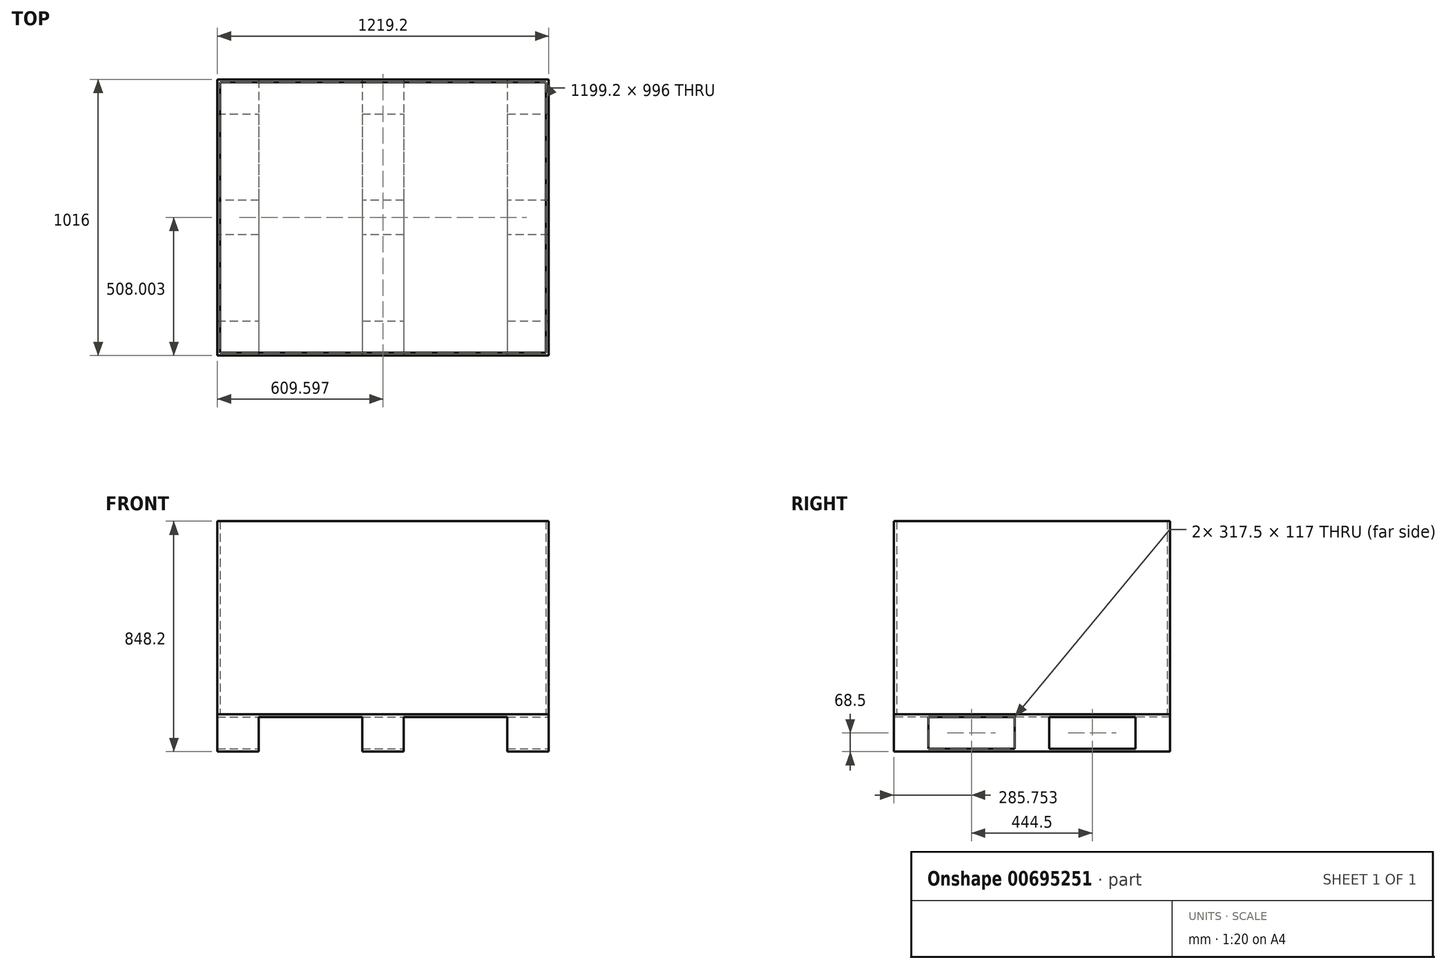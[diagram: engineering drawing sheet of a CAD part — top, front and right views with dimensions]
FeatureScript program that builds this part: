
annotation { "Feature Type Name" : "Feature", "Feature Type Description" : "" }
export const myFeature = defineFeature(function(context is Context, id is Id, definition is map)
    precondition{}
    {
        {
            var Q0;
            Q0=qCreatedBy(makeId("Top.planeOp"),FACE);
            var sketch = newSketch(context, id + "F0", { "sketchPlane" : qUnion([Q0])});
            skLineSegment(sketch, "E0.bottom", {"start": v(-1162.93, 976.86) * mm, "end": v(56.27, 976.86) * mm});
            skLineSegment(sketch, "E0.top", {"start": v(-1162.93, -39.14) * mm, "end": v(56.27, -39.14) * mm});
            skLineSegment(sketch, "E0.left", {"start": v(-1162.93, 976.86) * mm, "end": v(-1162.93, -39.14) * mm});
            skLineSegment(sketch, "E0.right", {"start": v(56.27, 976.86) * mm, "end": v(56.27, -39.14) * mm});
            skLineSegment(sketch, "E1.0", {"start": v(-1010.53, 976.86) * mm, "end": v(-1010.53, -39.14) * mm});
            skLineSegment(sketch, "E2.0", {"start": v(-96.13, 976.86) * mm, "end": v(-96.13, -39.14) * mm});
            skLineSegment(sketch, "E3.0", {"start": v(-1162.93, 849.86) * mm, "end": v(56.27, 849.86) * mm});
            skLineSegment(sketch, "E4.0", {"start": v(-1162.93, 87.86) * mm, "end": v(56.27, 87.86) * mm});
            skLineSegment(sketch, "E5", {"start": v(-553.33, 976.86) * mm, "end": v(-553.33, -39.14) * mm, "construction": true});
            skLineSegment(sketch, "E6", {"start": v(56.27, 468.86) * mm, "end": v(-1162.93, 468.86) * mm, "construction": true});
            skLineSegment(sketch, "E7.0", {"start": v(56.27, 532.36) * mm, "end": v(-1162.93, 532.36) * mm});
            skLineSegment(sketch, "E8.0", {"start": v(56.27, 405.36) * mm, "end": v(-1162.93, 405.36) * mm});
            skLineSegment(sketch, "E9.0", {"start": v(-629.53, 976.86) * mm, "end": v(-629.53, -39.14) * mm});
            skLineSegment(sketch, "E10.0", {"start": v(-477.13, 976.86) * mm, "end": v(-477.13, -39.14) * mm});
            skSolve(sketch);
        }
        {
            var Q0;
            {var subQ0=sQuery(id+"F0.wireOp",EDGE,"E0.left");var subQ1=sQuery(id+"F0.wireOp",EDGE,"E0.bottom");var subQ2=makeQuery(id+"F0.imprint","INTERSECT",VERTEX,{"derivedFrom":[subQ1,subQ0]});Q0=makeQuery(id+"F0.imprint","IMPRINT",FACE,{"disambiguationData":[TD([[makeQuery(id+"F0.imprint","IMPRINT",EDGE,{"disambiguationData":[TD([[subQ2,-1.0]])],"derivedFrom":subQ1}),-1.0]])]});}
            var Q1;
            {var subQ0=sQuery(id+"F0.wireOp",EDGE,"E1.0");var subQ1=sQuery(id+"F0.wireOp",EDGE,"E0.bottom");var subQ2=makeQuery(id+"F0.imprint","INTERSECT",VERTEX,{"derivedFrom":[subQ1,subQ0]});Q1=makeQuery(id+"F0.imprint","IMPRINT",FACE,{"disambiguationData":[TD([[makeQuery(id+"F0.imprint","IMPRINT",EDGE,{"disambiguationData":[TD([[subQ2,-1.0]])],"derivedFrom":subQ1}),-1.0]])]});}
            var Q2;
            {var subQ0=sQuery(id+"F0.wireOp",EDGE,"E9.0");var subQ1=sQuery(id+"F0.wireOp",EDGE,"E0.bottom");var subQ2=makeQuery(id+"F0.imprint","INTERSECT",VERTEX,{"derivedFrom":[subQ1,subQ0]});Q2=makeQuery(id+"F0.imprint","IMPRINT",FACE,{"disambiguationData":[TD([[makeQuery(id+"F0.imprint","IMPRINT",EDGE,{"disambiguationData":[TD([[subQ2,-1.0]])],"derivedFrom":subQ1}),-1.0]])]});}
            var Q3;
            {var subQ0=sQuery(id+"F0.wireOp",EDGE,"E2.0");var subQ1=sQuery(id+"F0.wireOp",EDGE,"E0.bottom");var subQ2=makeQuery(id+"F0.imprint","INTERSECT",VERTEX,{"derivedFrom":[subQ1,subQ0]});Q3=makeQuery(id+"F0.imprint","IMPRINT",FACE,{"disambiguationData":[TD([[makeQuery(id+"F0.imprint","IMPRINT",EDGE,{"disambiguationData":[TD([[subQ2,1.0]])],"derivedFrom":subQ1}),-1.0]])]});}
            var Q4;
            {var subQ0=sQuery(id+"F0.wireOp",EDGE,"E0.right");var subQ1=sQuery(id+"F0.wireOp",EDGE,"E0.bottom");var subQ2=makeQuery(id+"F0.imprint","INTERSECT",VERTEX,{"derivedFrom":[subQ1,subQ0]});Q4=makeQuery(id+"F0.imprint","IMPRINT",FACE,{"disambiguationData":[TD([[makeQuery(id+"F0.imprint","IMPRINT",EDGE,{"disambiguationData":[TD([[subQ2,1.0]])],"derivedFrom":subQ1}),-1.0]])]});}
            var Q5;
            {var subQ0=sQuery(id+"F0.wireOp",EDGE,"E3.0");var subQ1=sQuery(id+"F0.wireOp",EDGE,"E0.right");var subQ2=makeQuery(id+"F0.imprint","INTERSECT",VERTEX,{"derivedFrom":[subQ1,subQ0]});Q5=makeQuery(id+"F0.imprint","IMPRINT",FACE,{"disambiguationData":[TD([[makeQuery(id+"F0.imprint","IMPRINT",EDGE,{"disambiguationData":[TD([[subQ2,-1.0]])],"derivedFrom":subQ1}),-1.0]])]});}
            var Q6;
            {var subQ0=sQuery(id+"F0.wireOp",EDGE,"E3.0");var subQ1=sQuery(id+"F0.wireOp",EDGE,"E2.0");var subQ2=makeQuery(id+"F0.imprint","INTERSECT",VERTEX,{"derivedFrom":[subQ1,subQ0]});Q6=makeQuery(id+"F0.imprint","IMPRINT",FACE,{"disambiguationData":[TD([[makeQuery(id+"F0.imprint","IMPRINT",EDGE,{"disambiguationData":[TD([[subQ2,-1.0]])],"derivedFrom":subQ1}),-1.0]])]});}
            var Q7;
            {var subQ0=sQuery(id+"F0.wireOp",EDGE,"E9.0");var subQ1=sQuery(id+"F0.wireOp",EDGE,"E3.0");var subQ2=makeQuery(id+"F0.imprint","INTERSECT",VERTEX,{"derivedFrom":[subQ1,subQ0]});Q7=makeQuery(id+"F0.imprint","IMPRINT",FACE,{"disambiguationData":[TD([[makeQuery(id+"F0.imprint","IMPRINT",EDGE,{"disambiguationData":[TD([[subQ2,-1.0]])],"derivedFrom":subQ1}),-1.0]])]});}
            var Q8;
            {var subQ0=sQuery(id+"F0.wireOp",EDGE,"E3.0");var subQ1=sQuery(id+"F0.wireOp",EDGE,"E1.0");var subQ2=makeQuery(id+"F0.imprint","INTERSECT",VERTEX,{"derivedFrom":[subQ1,subQ0]});Q8=makeQuery(id+"F0.imprint","IMPRINT",FACE,{"disambiguationData":[TD([[makeQuery(id+"F0.imprint","IMPRINT",EDGE,{"disambiguationData":[TD([[subQ2,-1.0]])],"derivedFrom":subQ1}),1.0]])]});}
            var Q9;
            {var subQ0=sQuery(id+"F0.wireOp",EDGE,"E3.0");var subQ1=sQuery(id+"F0.wireOp",EDGE,"E0.left");var subQ2=makeQuery(id+"F0.imprint","INTERSECT",VERTEX,{"derivedFrom":[subQ1,subQ0]});Q9=makeQuery(id+"F0.imprint","IMPRINT",FACE,{"disambiguationData":[TD([[makeQuery(id+"F0.imprint","IMPRINT",EDGE,{"disambiguationData":[TD([[subQ2,-1.0]])],"derivedFrom":subQ1}),1.0]])]});}
            var Q10;
            {var subQ0=sQuery(id+"F0.wireOp",EDGE,"E0.left");var subQ1=sQuery(id+"F0.wireOp",EDGE,"E0.top");var subQ2=makeQuery(id+"F0.imprint","INTERSECT",VERTEX,{"derivedFrom":[subQ1,subQ0]});Q10=makeQuery(id+"F0.imprint","IMPRINT",FACE,{"disambiguationData":[TD([[makeQuery(id+"F0.imprint","IMPRINT",EDGE,{"disambiguationData":[TD([[subQ2,-1.0]])],"derivedFrom":subQ1}),1.0]])]});}
            var Q11;
            {var subQ0=sQuery(id+"F0.wireOp",EDGE,"E4.0");var subQ1=sQuery(id+"F0.wireOp",EDGE,"E0.left");var subQ2=makeQuery(id+"F0.imprint","INTERSECT",VERTEX,{"derivedFrom":[subQ1,subQ0]});Q11=makeQuery(id+"F0.imprint","IMPRINT",FACE,{"disambiguationData":[TD([[makeQuery(id+"F0.imprint","IMPRINT",EDGE,{"disambiguationData":[TD([[subQ2,1.0]])],"derivedFrom":subQ1}),1.0]])]});}
            var Q12;
            {var subQ0=sQuery(id+"F0.wireOp",EDGE,"E1.0");var subQ1=sQuery(id+"F0.wireOp",EDGE,"E0.top");var subQ2=makeQuery(id+"F0.imprint","INTERSECT",VERTEX,{"derivedFrom":[subQ1,subQ0]});Q12=makeQuery(id+"F0.imprint","IMPRINT",FACE,{"disambiguationData":[TD([[makeQuery(id+"F0.imprint","IMPRINT",EDGE,{"disambiguationData":[TD([[subQ2,-1.0]])],"derivedFrom":subQ1}),1.0]])]});}
            var Q13;
            {var subQ0=sQuery(id+"F0.wireOp",EDGE,"E8.0");var subQ1=sQuery(id+"F0.wireOp",EDGE,"E2.0");var subQ2=makeQuery(id+"F0.imprint","INTERSECT",VERTEX,{"derivedFrom":[subQ1,subQ0]});Q13=makeQuery(id+"F0.imprint","IMPRINT",FACE,{"disambiguationData":[TD([[makeQuery(id+"F0.imprint","IMPRINT",EDGE,{"disambiguationData":[TD([[subQ2,-1.0]])],"derivedFrom":subQ1}),-1.0]])]});}
            var Q14;
            {var subQ0=sQuery(id+"F0.wireOp",EDGE,"E8.0");var subQ1=sQuery(id+"F0.wireOp",EDGE,"E1.0");var subQ2=makeQuery(id+"F0.imprint","INTERSECT",VERTEX,{"derivedFrom":[subQ1,subQ0]});Q14=makeQuery(id+"F0.imprint","IMPRINT",FACE,{"disambiguationData":[TD([[makeQuery(id+"F0.imprint","IMPRINT",EDGE,{"disambiguationData":[TD([[subQ2,-1.0]])],"derivedFrom":subQ1}),1.0]])]});}
            var Q15;
            {var subQ0=sQuery(id+"F0.wireOp",EDGE,"E2.0");var subQ1=sQuery(id+"F0.wireOp",EDGE,"E0.top");var subQ2=makeQuery(id+"F0.imprint","INTERSECT",VERTEX,{"derivedFrom":[subQ1,subQ0]});Q15=makeQuery(id+"F0.imprint","IMPRINT",FACE,{"disambiguationData":[TD([[makeQuery(id+"F0.imprint","IMPRINT",EDGE,{"disambiguationData":[TD([[subQ2,1.0]])],"derivedFrom":subQ1}),1.0]])]});}
            var Q16;
            {var subQ0=sQuery(id+"F0.wireOp",EDGE,"E4.0");var subQ1=sQuery(id+"F0.wireOp",EDGE,"E0.right");var subQ2=makeQuery(id+"F0.imprint","INTERSECT",VERTEX,{"derivedFrom":[subQ1,subQ0]});Q16=makeQuery(id+"F0.imprint","IMPRINT",FACE,{"disambiguationData":[TD([[makeQuery(id+"F0.imprint","IMPRINT",EDGE,{"disambiguationData":[TD([[subQ2,1.0]])],"derivedFrom":subQ1}),-1.0]])]});}
            var Q17;
            {var subQ0=sQuery(id+"F0.wireOp",EDGE,"E7.0");var subQ1=sQuery(id+"F0.wireOp",EDGE,"E0.left");var subQ2=makeQuery(id+"F0.imprint","INTERSECT",VERTEX,{"derivedFrom":[subQ1,subQ0]});Q17=makeQuery(id+"F0.imprint","IMPRINT",FACE,{"disambiguationData":[TD([[makeQuery(id+"F0.imprint","IMPRINT",EDGE,{"disambiguationData":[TD([[subQ2,-1.0]])],"derivedFrom":subQ1}),1.0]])]});}
            var Q18;
            {var subQ0=sQuery(id+"F0.wireOp",EDGE,"E7.0");var subQ1=sQuery(id+"F0.wireOp",EDGE,"E1.0");var subQ2=makeQuery(id+"F0.imprint","INTERSECT",VERTEX,{"derivedFrom":[subQ1,subQ0]});Q18=makeQuery(id+"F0.imprint","IMPRINT",FACE,{"disambiguationData":[TD([[makeQuery(id+"F0.imprint","IMPRINT",EDGE,{"disambiguationData":[TD([[subQ2,-1.0]])],"derivedFrom":subQ1}),1.0]])]});}
            var Q19;
            {var subQ0=sQuery(id+"F0.wireOp",EDGE,"E10.0");var subQ1=sQuery(id+"F0.wireOp",EDGE,"E7.0");var subQ2=makeQuery(id+"F0.imprint","INTERSECT",VERTEX,{"derivedFrom":[subQ1,subQ0]});Q19=makeQuery(id+"F0.imprint","IMPRINT",FACE,{"disambiguationData":[TD([[makeQuery(id+"F0.imprint","IMPRINT",EDGE,{"disambiguationData":[TD([[subQ2,-1.0]])],"derivedFrom":subQ1}),1.0]])]});}
            var Q20;
            {var subQ0=sQuery(id+"F0.wireOp",EDGE,"E7.0");var subQ1=sQuery(id+"F0.wireOp",EDGE,"E2.0");var subQ2=makeQuery(id+"F0.imprint","INTERSECT",VERTEX,{"derivedFrom":[subQ1,subQ0]});Q20=makeQuery(id+"F0.imprint","IMPRINT",FACE,{"disambiguationData":[TD([[makeQuery(id+"F0.imprint","IMPRINT",EDGE,{"disambiguationData":[TD([[subQ2,-1.0]])],"derivedFrom":subQ1}),-1.0]])]});}
            var Q21;
            {var subQ0=sQuery(id+"F0.wireOp",EDGE,"E9.0");var subQ1=sQuery(id+"F0.wireOp",EDGE,"E4.0");var subQ2=makeQuery(id+"F0.imprint","INTERSECT",VERTEX,{"derivedFrom":[subQ1,subQ0]});Q21=makeQuery(id+"F0.imprint","IMPRINT",FACE,{"disambiguationData":[TD([[makeQuery(id+"F0.imprint","IMPRINT",EDGE,{"disambiguationData":[TD([[subQ2,-1.0]])],"derivedFrom":subQ1}),1.0]])]});}
            var Q22;
            {var subQ0=sQuery(id+"F0.wireOp",EDGE,"E7.0");var subQ1=sQuery(id+"F0.wireOp",EDGE,"E0.right");var subQ2=makeQuery(id+"F0.imprint","INTERSECT",VERTEX,{"derivedFrom":[subQ1,subQ0]});Q22=makeQuery(id+"F0.imprint","IMPRINT",FACE,{"disambiguationData":[TD([[makeQuery(id+"F0.imprint","IMPRINT",EDGE,{"disambiguationData":[TD([[subQ2,-1.0]])],"derivedFrom":subQ1}),-1.0]])]});}
            var Q23;
            {var subQ0=sQuery(id+"F0.wireOp",EDGE,"E9.0");var subQ1=sQuery(id+"F0.wireOp",EDGE,"E0.top");var subQ2=makeQuery(id+"F0.imprint","INTERSECT",VERTEX,{"derivedFrom":[subQ1,subQ0]});Q23=makeQuery(id+"F0.imprint","IMPRINT",FACE,{"disambiguationData":[TD([[makeQuery(id+"F0.imprint","IMPRINT",EDGE,{"disambiguationData":[TD([[subQ2,-1.0]])],"derivedFrom":subQ1}),1.0]])]});}
            var Q24;
            {var subQ0=sQuery(id+"F0.wireOp",EDGE,"E0.right");var subQ1=sQuery(id+"F0.wireOp",EDGE,"E0.top");var subQ2=makeQuery(id+"F0.imprint","INTERSECT",VERTEX,{"derivedFrom":[subQ1,subQ0]});Q24=makeQuery(id+"F0.imprint","IMPRINT",FACE,{"disambiguationData":[TD([[makeQuery(id+"F0.imprint","IMPRINT",EDGE,{"disambiguationData":[TD([[subQ2,1.0]])],"derivedFrom":subQ1}),1.0]])]});}
            extrude(context, id + "F1", {"entities" : qUnion([Q0, Q1, Q2, Q3, Q4, Q5, Q6, Q7, Q8, Q9, Q10, Q11, Q12, Q13, Q14, Q15, Q16, Q17, Q18, Q19, Q20, Q21, Q22, Q23, Q24]), "depth" : 10 * mm, "offsetDistance" : 25 * mm});
        }
        {
            var Q0;
            {var subQ0=sQuery(id+"F0.wireOp",EDGE,"E0.left");var subQ1=sQuery(id+"F0.wireOp",EDGE,"E0.top");var subQ2=makeQuery(id+"F0.imprint","INTERSECT",VERTEX,{"derivedFrom":[subQ1,subQ0]});Q0=makeQuery(id+"F0.imprint","IMPRINT",FACE,{"disambiguationData":[TD([[makeQuery(id+"F0.imprint","IMPRINT",EDGE,{"disambiguationData":[TD([[subQ2,-1.0]])],"derivedFrom":subQ1}),1.0]])]});}
            var Q1;
            {var subQ0=sQuery(id+"F0.wireOp",EDGE,"E9.0");var subQ1=sQuery(id+"F0.wireOp",EDGE,"E0.top");var subQ2=makeQuery(id+"F0.imprint","INTERSECT",VERTEX,{"derivedFrom":[subQ1,subQ0]});Q1=makeQuery(id+"F0.imprint","IMPRINT",FACE,{"disambiguationData":[TD([[makeQuery(id+"F0.imprint","IMPRINT",EDGE,{"disambiguationData":[TD([[subQ2,-1.0]])],"derivedFrom":subQ1}),1.0]])]});}
            var Q2;
            {var subQ0=sQuery(id+"F0.wireOp",EDGE,"E0.right");var subQ1=sQuery(id+"F0.wireOp",EDGE,"E0.top");var subQ2=makeQuery(id+"F0.imprint","INTERSECT",VERTEX,{"derivedFrom":[subQ1,subQ0]});Q2=makeQuery(id+"F0.imprint","IMPRINT",FACE,{"disambiguationData":[TD([[makeQuery(id+"F0.imprint","IMPRINT",EDGE,{"disambiguationData":[TD([[subQ2,1.0]])],"derivedFrom":subQ1}),1.0]])]});}
            var Q3;
            {var subQ0=sQuery(id+"F0.wireOp",EDGE,"E7.0");var subQ1=sQuery(id+"F0.wireOp",EDGE,"E0.right");var subQ2=makeQuery(id+"F0.imprint","INTERSECT",VERTEX,{"derivedFrom":[subQ1,subQ0]});Q3=makeQuery(id+"F0.imprint","IMPRINT",FACE,{"disambiguationData":[TD([[makeQuery(id+"F0.imprint","IMPRINT",EDGE,{"disambiguationData":[TD([[subQ2,-1.0]])],"derivedFrom":subQ1}),-1.0]])]});}
            var Q4;
            {var subQ0=sQuery(id+"F0.wireOp",EDGE,"E10.0");var subQ1=sQuery(id+"F0.wireOp",EDGE,"E7.0");var subQ2=makeQuery(id+"F0.imprint","INTERSECT",VERTEX,{"derivedFrom":[subQ1,subQ0]});Q4=makeQuery(id+"F0.imprint","IMPRINT",FACE,{"disambiguationData":[TD([[makeQuery(id+"F0.imprint","IMPRINT",EDGE,{"disambiguationData":[TD([[subQ2,-1.0]])],"derivedFrom":subQ1}),1.0]])]});}
            var Q5;
            {var subQ0=sQuery(id+"F0.wireOp",EDGE,"E7.0");var subQ1=sQuery(id+"F0.wireOp",EDGE,"E0.left");var subQ2=makeQuery(id+"F0.imprint","INTERSECT",VERTEX,{"derivedFrom":[subQ1,subQ0]});Q5=makeQuery(id+"F0.imprint","IMPRINT",FACE,{"disambiguationData":[TD([[makeQuery(id+"F0.imprint","IMPRINT",EDGE,{"disambiguationData":[TD([[subQ2,-1.0]])],"derivedFrom":subQ1}),1.0]])]});}
            var Q6;
            {var subQ0=sQuery(id+"F0.wireOp",EDGE,"E0.left");var subQ1=sQuery(id+"F0.wireOp",EDGE,"E0.bottom");var subQ2=makeQuery(id+"F0.imprint","INTERSECT",VERTEX,{"derivedFrom":[subQ1,subQ0]});Q6=makeQuery(id+"F0.imprint","IMPRINT",FACE,{"disambiguationData":[TD([[makeQuery(id+"F0.imprint","IMPRINT",EDGE,{"disambiguationData":[TD([[subQ2,-1.0]])],"derivedFrom":subQ1}),-1.0]])]});}
            var Q7;
            {var subQ0=sQuery(id+"F0.wireOp",EDGE,"E9.0");var subQ1=sQuery(id+"F0.wireOp",EDGE,"E0.bottom");var subQ2=makeQuery(id+"F0.imprint","INTERSECT",VERTEX,{"derivedFrom":[subQ1,subQ0]});Q7=makeQuery(id+"F0.imprint","IMPRINT",FACE,{"disambiguationData":[TD([[makeQuery(id+"F0.imprint","IMPRINT",EDGE,{"disambiguationData":[TD([[subQ2,-1.0]])],"derivedFrom":subQ1}),-1.0]])]});}
            var Q8;
            {var subQ0=sQuery(id+"F0.wireOp",EDGE,"E0.right");var subQ1=sQuery(id+"F0.wireOp",EDGE,"E0.bottom");var subQ2=makeQuery(id+"F0.imprint","INTERSECT",VERTEX,{"derivedFrom":[subQ1,subQ0]});Q8=makeQuery(id+"F0.imprint","IMPRINT",FACE,{"disambiguationData":[TD([[makeQuery(id+"F0.imprint","IMPRINT",EDGE,{"disambiguationData":[TD([[subQ2,1.0]])],"derivedFrom":subQ1}),-1.0]])]});}
            extrude(context, id + "F2", {"entities" : qUnion([Q0, Q1, Q2, Q3, Q4, Q5, Q6, Q7, Q8]), "operationType" : NewBodyOperationType.ADD, "oppositeDirection" : true, "depth" : 127 * mm, "offsetDistance" : 25 * mm});
        }
        {
            var Q0;
            {var subQ0=sQuery(id+"F0.wireOp",EDGE,"E4.0");var subQ1=sQuery(id+"F0.wireOp",EDGE,"E0.left");var subQ2=makeQuery(id+"F0.imprint","INTERSECT",VERTEX,{"derivedFrom":[subQ1,subQ0]});Q0=makeQuery(id+"F0.imprint","IMPRINT",FACE,{"disambiguationData":[TD([[makeQuery(id+"F0.imprint","IMPRINT",EDGE,{"disambiguationData":[TD([[subQ2,1.0]])],"derivedFrom":subQ1}),1.0]])]});}
            var Q1;
            {var subQ0=sQuery(id+"F0.wireOp",EDGE,"E9.0");var subQ1=sQuery(id+"F0.wireOp",EDGE,"E4.0");var subQ2=makeQuery(id+"F0.imprint","INTERSECT",VERTEX,{"derivedFrom":[subQ1,subQ0]});Q1=makeQuery(id+"F0.imprint","IMPRINT",FACE,{"disambiguationData":[TD([[makeQuery(id+"F0.imprint","IMPRINT",EDGE,{"disambiguationData":[TD([[subQ2,-1.0]])],"derivedFrom":subQ1}),1.0]])]});}
            var Q2;
            {var subQ0=sQuery(id+"F0.wireOp",EDGE,"E4.0");var subQ1=sQuery(id+"F0.wireOp",EDGE,"E0.right");var subQ2=makeQuery(id+"F0.imprint","INTERSECT",VERTEX,{"derivedFrom":[subQ1,subQ0]});Q2=makeQuery(id+"F0.imprint","IMPRINT",FACE,{"disambiguationData":[TD([[makeQuery(id+"F0.imprint","IMPRINT",EDGE,{"disambiguationData":[TD([[subQ2,1.0]])],"derivedFrom":subQ1}),-1.0]])]});}
            var Q3;
            {var subQ0=sQuery(id+"F0.wireOp",EDGE,"E3.0");var subQ1=sQuery(id+"F0.wireOp",EDGE,"E0.right");var subQ2=makeQuery(id+"F0.imprint","INTERSECT",VERTEX,{"derivedFrom":[subQ1,subQ0]});Q3=makeQuery(id+"F0.imprint","IMPRINT",FACE,{"disambiguationData":[TD([[makeQuery(id+"F0.imprint","IMPRINT",EDGE,{"disambiguationData":[TD([[subQ2,-1.0]])],"derivedFrom":subQ1}),-1.0]])]});}
            var Q4;
            {var subQ0=sQuery(id+"F0.wireOp",EDGE,"E9.0");var subQ1=sQuery(id+"F0.wireOp",EDGE,"E3.0");var subQ2=makeQuery(id+"F0.imprint","INTERSECT",VERTEX,{"derivedFrom":[subQ1,subQ0]});Q4=makeQuery(id+"F0.imprint","IMPRINT",FACE,{"disambiguationData":[TD([[makeQuery(id+"F0.imprint","IMPRINT",EDGE,{"disambiguationData":[TD([[subQ2,-1.0]])],"derivedFrom":subQ1}),-1.0]])]});}
            var Q5;
            {var subQ0=sQuery(id+"F0.wireOp",EDGE,"E3.0");var subQ1=sQuery(id+"F0.wireOp",EDGE,"E0.left");var subQ2=makeQuery(id+"F0.imprint","INTERSECT",VERTEX,{"derivedFrom":[subQ1,subQ0]});Q5=makeQuery(id+"F0.imprint","IMPRINT",FACE,{"disambiguationData":[TD([[makeQuery(id+"F0.imprint","IMPRINT",EDGE,{"disambiguationData":[TD([[subQ2,-1.0]])],"derivedFrom":subQ1}),1.0]])]});}
            extrude(context, id + "F3", {"entities" : qUnion([Q0, Q1, Q2, Q3, Q4, Q5]), "operationType" : NewBodyOperationType.ADD, "oppositeDirection" : true, "depth" : 127 * mm, "offsetDistance" : 25 * mm, "hasSecondDirection" : true, "secondDirectionOppositeDirection" : true, "secondDirectionDepth" : 117 * mm});
        }
        {
            var Q0;
            Q0=makeQuery(id+"F1.opExtrude","CAP_FACE",FACE,{"disambiguationData":[OSD([sQuery(id+"F0.wireOp",EDGE,"E0.bottom"),sQuery(id+"F0.wireOp",EDGE,"E0.top"),sQuery(id+"F0.wireOp",EDGE,"E0.left"),sQuery(id+"F0.wireOp",EDGE,"E0.right")])],"isStart":false});
            var sketch = newSketch(context, id + "F4", { "sketchPlane" : qUnion([Q0])});
            skLineSegment(sketch, "E11.0", {"start": v(-1152.93, 966.86) * mm, "end": v(-1152.93, -29.14) * mm});
            skLineSegment(sketch, "E11.1", {"start": v(-1152.93, 966.86) * mm, "end": v(46.27, 966.86) * mm});
            skLineSegment(sketch, "E11.2", {"start": v(46.27, 966.86) * mm, "end": v(46.27, -29.14) * mm});
            skLineSegment(sketch, "E11.3", {"start": v(-1152.93, -29.14) * mm, "end": v(46.27, -29.14) * mm});
            skSolve(sketch);
        }
        {
            var Q0;
            Q0=makeQuery(id+"F4.imprint","IMPRINT",FACE,{"disambiguationData":[TD([[makeQuery(id+"F4.imprint","IMPRINT",EDGE,{"derivedFrom":sQuery(id+"F4.wireOp",EDGE,"E11.0")}),-1.0]])]});
            extrude(context, id + "F5", {"entities" : qUnion([Q0]), "depth" : 711.2 * mm, "offsetDistance" : 25 * mm});
        }
    });
